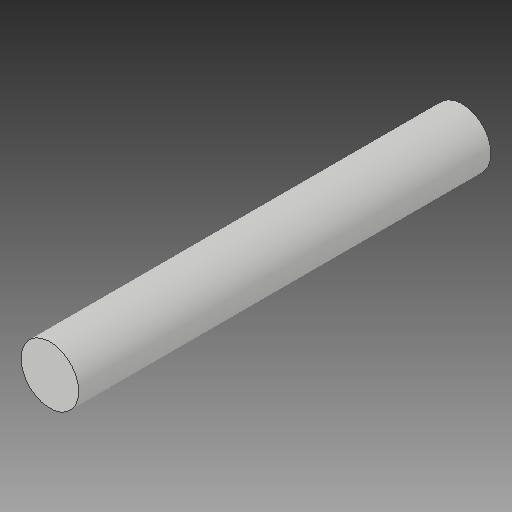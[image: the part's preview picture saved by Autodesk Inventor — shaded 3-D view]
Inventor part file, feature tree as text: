
AUTODESK INVENTOR PART (.ipt)
format: ipt  version: 2019 (Build 230136000, 136)  size: 90,112 bytes
history: native  units: mm
features: extrude x1, sketch x1
ambient origin geometry x8: Origin, YZ Plane, XZ Plane, XY Plane, X Axis, Y Axis, Z Axis, Center Point
bodies: Solid1 (feature_tree)
feature tree (2):
  extrude  "Extrusion1"  Depth=50.0mm TaperAngle=0.0deg
  sketch  "Sketch1"  dims[d0=7.0mm d1=50.0mm d2=0.0mm]
